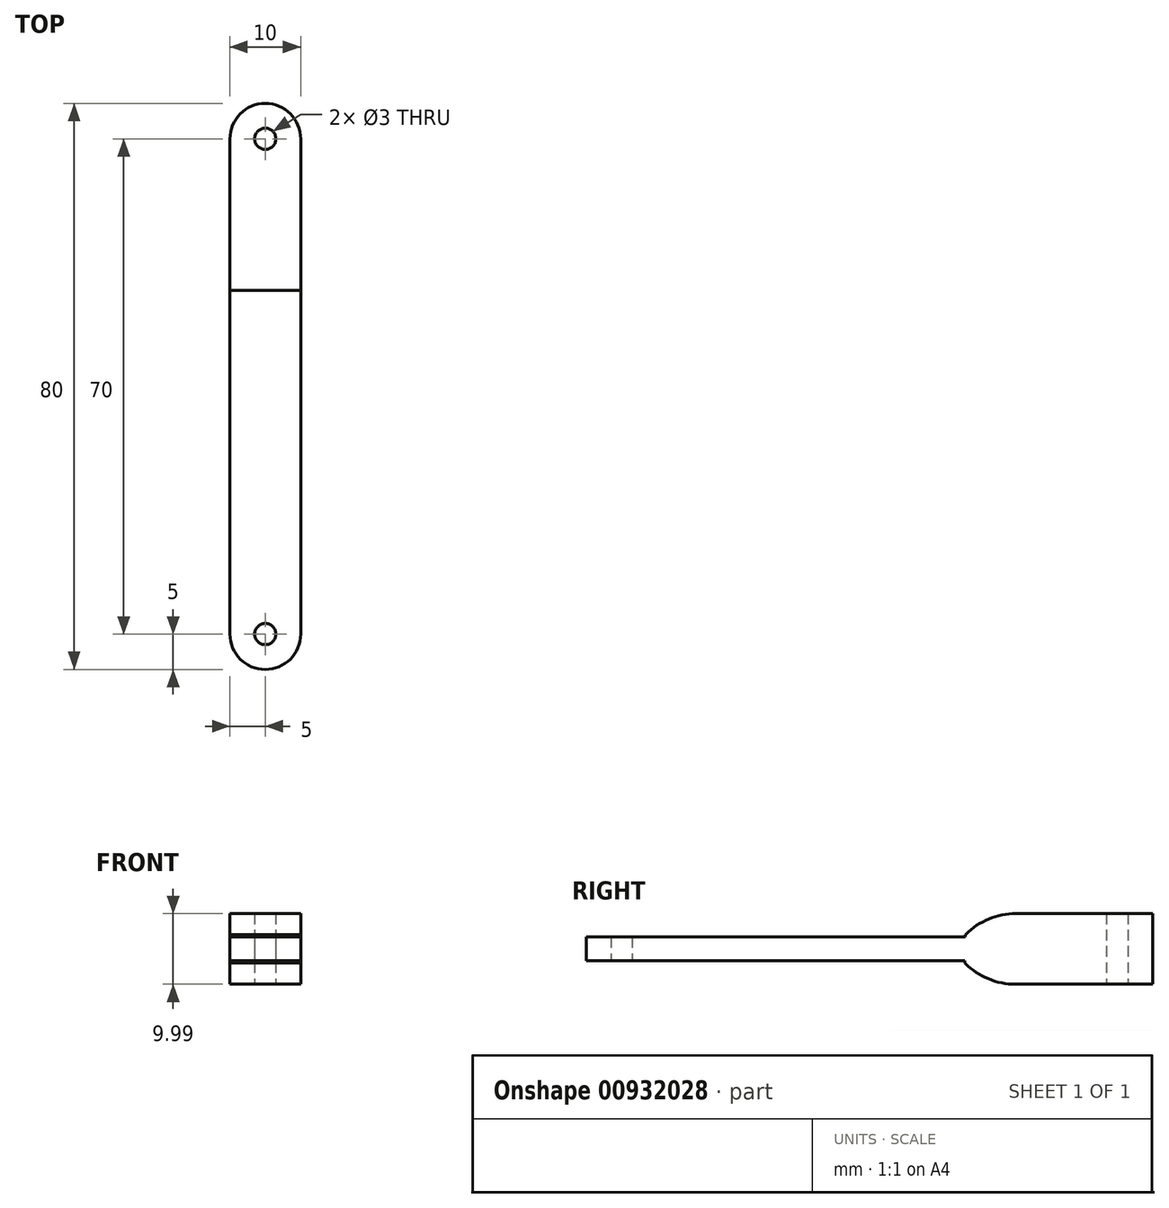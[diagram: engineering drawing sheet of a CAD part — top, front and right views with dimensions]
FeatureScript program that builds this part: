
annotation { "Feature Type Name" : "Feature", "Feature Type Description" : "" }
export const myFeature = defineFeature(function(context is Context, id is Id, definition is map)
    precondition{}
    {
        {
            var Q0;
            Q0=qCreatedBy(makeId("Top.planeOp"),FACE);
            var sketch = newSketch(context, id + "F0", { "sketchPlane" : qUnion([Q0])});
            skLineSegment(sketch, "E0.left", {"start": v(5, -35) * mm, "end": v(5, 35) * mm});
            skLineSegment(sketch, "E0.right", {"start": v(-5, -35) * mm, "end": v(-5, 35) * mm});
            skPoint(sketch, "E0.middle", {"position": v(0, 0) * mm});
            skArc(sketch, "E1", {"start": v(5, 35) * mm, "mid": v(0, 40) * mm, "end": v(-5, 35) * mm});
            skArc(sketch, "E2", {"start": v(-5, -35) * mm, "mid": v(0, -40) * mm, "end": v(5, -35) * mm});
            skCircle(sketch, "E3", {"center": v(0, 35) * mm, "radius": 1.5 * mm});
            skCircle(sketch, "E4", {"center": v(0, -35) * mm, "radius": 1.5 * mm});
            skSolve(sketch);
        }
        {
            var Q0;
            Q0=makeQuery(id+"F0.imprint","IMPRINT",FACE,{"disambiguationData":[TD([[makeQuery(id+"F0.imprint","IMPRINT",EDGE,{"derivedFrom":sQuery(id+"F0.wireOp",EDGE,"E0.left")}),1.0]])]});
            extrude(context, id + "F1", {"entities" : qUnion([Q0]), "depth" : 3.33 * mm, "offsetDistance" : 25 * mm});
        }
        {
            var Q0;
            Q0=makeQuery(id+"F1.opExtrude","CAP_FACE",FACE,{"disambiguationData":[OSD([sQuery(id+"F0.wireOp",EDGE,"E0.left"),sQuery(id+"F0.wireOp",EDGE,"E0.right"),sQuery(id+"F0.wireOp",EDGE,"E1"),sQuery(id+"F0.wireOp",EDGE,"E2"),sQuery(id+"F0.wireOp",EDGE,"E3"),sQuery(id+"F0.wireOp",EDGE,"E4")])],"isStart":false});
            var sketch = newSketch(context, id + "F2", { "sketchPlane" : qUnion([Q0])});
            skLineSegment(sketch, "E5", {"start": v(-5, 13.57) * mm, "end": v(5, 13.57) * mm});
            skSolve(sketch);
        }
        {
            var Q0;
            Q0=makeQuery(id+"F1.opExtrude","CAP_FACE",FACE,{"disambiguationData":[OSD([sQuery(id+"F0.wireOp",EDGE,"E0.left"),sQuery(id+"F0.wireOp",EDGE,"E0.right"),sQuery(id+"F0.wireOp",EDGE,"E1"),sQuery(id+"F0.wireOp",EDGE,"E2"),sQuery(id+"F0.wireOp",EDGE,"E3"),sQuery(id+"F0.wireOp",EDGE,"E4")])],"isStart":true});
            var sketch = newSketch(context, id + "F3", { "sketchPlane" : qUnion([Q0])});
            skLineSegment(sketch, "E6", {"start": v(5, -13.5) * mm, "end": v(-5, -13.5) * mm});
            skSolve(sketch);
        }
        {
            var Q0;
            {var subQ2=sQuery(id+"F3.wireOp",EDGE,"E6");Q0=makeQuery(id+"F3.imprint","IMPRINT",FACE,{"disambiguationData":[TD([[makeQuery(id+"F3.imprint","IMPRINT",EDGE,{"derivedFrom":subQ2}),1.0]])]});}
            extrude(context, id + "F4", {"entities" : qUnion([Q0]), "operationType" : NewBodyOperationType.ADD, "depth" : 3.33 * mm, "offsetDistance" : 25 * mm});
        }
        {
            var Q0;
            {var subQ2=sQuery(id+"F2.wireOp",EDGE,"E5");Q0=makeQuery(id+"F2.imprint","IMPRINT",FACE,{"disambiguationData":[TD([[makeQuery(id+"F2.imprint","IMPRINT",EDGE,{"derivedFrom":subQ2}),1.0]])]});}
            extrude(context, id + "F5", {"entities" : qUnion([Q0]), "operationType" : NewBodyOperationType.ADD, "depth" : 3.33 * mm, "offsetDistance" : 25 * mm});
        }
        {
            var Q0;
            Q0=makeQuery(id+"F5.opExtrude","CAP_EDGE",EDGE,{"disambiguationData":[OSD([sQuery(id+"F2.wireOp",EDGE,"E5")])],"isStart":false});
            chamfer(context, id + "F6", {"entities" : qUnion([Q0]), "width" : 3 * mm, "tangentPropagation" : true});
        }
        {
            var Q0;
            {var subQ0=sQuery(id+"F2.wireOp",EDGE,"E5");Q0=makeQuery(id+"F6.opChamfer","BLEND_EDGE",EDGE,{"blendedFrom":[makeQuery(id+"F5.opExtrude","CAP_EDGE",EDGE,{"disambiguationData":[OSD([subQ0])],"isStart":false}),makeQuery(id+"F5.opExtrude","CAP_FACE",FACE,{"disambiguationData":[OSD([sQuery(id+"F0.wireOp",EDGE,"E0.left"),sQuery(id+"F0.wireOp",EDGE,"E0.right"),sQuery(id+"F0.wireOp",EDGE,"E1"),sQuery(id+"F0.wireOp",EDGE,"E3"),subQ0])],"isStart":false})],"blendedInto":[makeQuery(id+"F5.opExtrude","CAP_FACE",FACE,{"disambiguationData":[OSD([sQuery(id+"F0.wireOp",EDGE,"E0.left"),sQuery(id+"F0.wireOp",EDGE,"E0.right"),sQuery(id+"F0.wireOp",EDGE,"E1"),sQuery(id+"F0.wireOp",EDGE,"E3"),subQ0])],"isStart":false})]});}
            fillet(context, id + "F7", {"entities" : qUnion([Q0]), "radius" : 10 * mm, "tangentPropagation" : true, "allowEdgeOverflow" : false});
        }
        {
            var Q0;
            Q0=makeQuery(id+"F4.opExtrude","CAP_EDGE",EDGE,{"disambiguationData":[OSD([sQuery(id+"F3.wireOp",EDGE,"E6")])],"isStart":false});
            chamfer(context, id + "F8", {"entities" : qUnion([Q0]), "width" : 3 * mm, "tangentPropagation" : true});
        }
        {
            var Q0;
            {var subQ0=sQuery(id+"F3.wireOp",EDGE,"E6");Q0=makeQuery(id+"F8.opChamfer","BLEND_EDGE",EDGE,{"blendedFrom":[makeQuery(id+"F4.opExtrude","CAP_EDGE",EDGE,{"disambiguationData":[OSD([subQ0])],"isStart":false}),makeQuery(id+"F4.opExtrude","CAP_FACE",FACE,{"disambiguationData":[OSD([sQuery(id+"F0.wireOp",EDGE,"E0.left"),sQuery(id+"F0.wireOp",EDGE,"E0.right"),sQuery(id+"F0.wireOp",EDGE,"E1"),sQuery(id+"F0.wireOp",EDGE,"E3"),subQ0])],"isStart":false})],"blendedInto":[makeQuery(id+"F4.opExtrude","CAP_FACE",FACE,{"disambiguationData":[OSD([sQuery(id+"F0.wireOp",EDGE,"E0.left"),sQuery(id+"F0.wireOp",EDGE,"E0.right"),sQuery(id+"F0.wireOp",EDGE,"E1"),sQuery(id+"F0.wireOp",EDGE,"E3"),subQ0])],"isStart":false})]});}
            fillet(context, id + "F9", {"entities" : qUnion([Q0]), "radius" : 10 * mm, "tangentPropagation" : true, "allowEdgeOverflow" : false});
        }
    });
